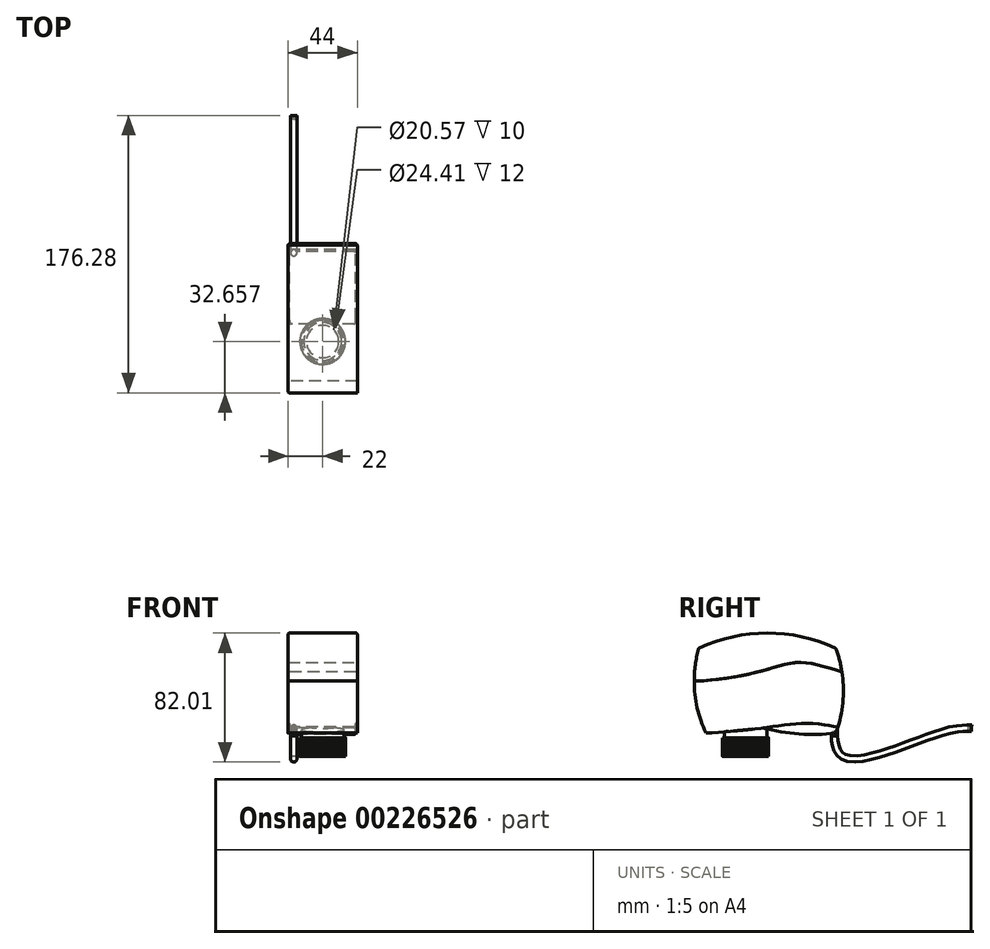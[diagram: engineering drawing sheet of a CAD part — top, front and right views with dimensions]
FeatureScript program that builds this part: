
annotation { "Feature Type Name" : "Feature", "Feature Type Description" : "" }
export const myFeature = defineFeature(function(context is Context, id is Id, definition is map)
    precondition{}
    {
        {
            var Q0;
            Q0=qCreatedBy(makeId("Right.planeOp"),FACE);
            var sketch = newSketch(context, id + "F0", { "sketchPlane" : qUnion([Q0])});
            skArc(sketch, "E0", {"start": v(-40.88, 27.1) * mm, "mid": v(-43.48, -0.31) * mm, "end": v(-36.3, -26.9) * mm});
            skArc(sketch, "E1", {"start": v(46.12, 27.1) * mm, "mid": v(2.62, 36.69) * mm, "end": v(-40.88, 27.1) * mm});
            skArc(sketch, "E2", {"start": v(46.12, -26.9) * mm, "mid": v(50.98, 0.1) * mm, "end": v(46.12, 27.1) * mm});
            skLineSegment(sketch, "E3", {"start": v(-36.3, -26.9) * mm, "end": v(46.12, -26.9) * mm, "construction": true});
            skFitSpline(sketch, "E4", {"points": [v(-43.75, 6.1) * mm, v(0, 12.84) * mm, v(24.24, 17.97) * mm, v(50.05, 12.1) * mm], "startDerivative": vector(120.11, 3.83) * mm, "endDerivative": vector(83.49, -22.87) * mm});
            skFitSpline(sketch, "E5", {"points": [v(-36.3, -26.9) * mm, v(0, -23.58) * mm, v(32.41, -20.85) * mm, v(47.43, -23.06) * mm, v(47.45, -23) * mm], "startDerivative": vector(96.75, 6.97) * mm, "endDerivative": vector(-0.56, 4.09) * mm});
            skSolve(sketch);
        }
        {
            var Q0;
            {var subQ0=sQuery(id+"F0.wireOp",EDGE,"E1");Q0=makeQuery(id+"F0.imprint","IMPRINT",FACE,{"disambiguationData":[TD([[makeQuery(id+"F0.imprint","IMPRINT",EDGE,{"derivedFrom":subQ0}),1.0]])]});}
            extrude(context, id + "F1", {"entities" : qUnion([Q0]), "endBound" : BoundingType.SYMMETRIC, "depth" : 44 * mm});
        }
        {
            var Q0;
            {var subQ0=sQuery(id+"F0.wireOp",EDGE,"E4");Q0=makeQuery(id+"F0.imprint","IMPRINT",FACE,{"disambiguationData":[TD([[makeQuery(id+"F0.imprint","IMPRINT",EDGE,{"derivedFrom":subQ0}),-1.0]])]});}
            extrude(context, id + "F2", {"entities" : qUnion([Q0]), "endBound" : BoundingType.SYMMETRIC, "depth" : 44 * mm});
        }
        {
            var Q0;
            Q0=qCreatedBy(makeId("Right.planeOp"),FACE);
            var sketch = newSketch(context, id + "F3", { "sketchPlane" : qUnion([Q0])});
            skArc(sketch, "E6", {"start": v(0, -23.58) * mm, "mid": v(22.9, -27.46) * mm, "end": v(46.12, -26.9) * mm});
            skLineSegment(sketch, "E7", {"start": v(46.12, -26.9) * mm, "end": v(47.43, -23.06) * mm});
            skLineSegment(sketch, "E8", {"start": v(0, -23.58) * mm, "end": v(31.62, -13.02) * mm});
            skLineSegment(sketch, "E9", {"start": v(31.62, -13.02) * mm, "end": v(47.43, -23.06) * mm});
            skSolve(sketch);
        }
        {
            var Q0;
            Q0 = qSketchRegion(id + "F3", true);
            extrude(context, id + "F4", {"entities" : qUnion([Q0]), "operationType" : NewBodyOperationType.ADD, "endBound" : BoundingType.SYMMETRIC, "depth" : 42 * mm});
        }
        {
            var Q0;
            Q0=qCreatedBy(makeId("Right.planeOp"),FACE);
            var sketch = newSketch(context, id + "F5", { "sketchPlane" : qUnion([Q0])});
            skLineSegment(sketch, "E10", {"start": v(-11.1, 0.62) * mm, "end": v(-11.1, -57.57) * mm, "construction": true});
            skLineSegment(sketch, "E11", {"start": v(2.4, -19.81) * mm, "end": v(2.4, -29.81) * mm});
            skLineSegment(sketch, "E12", {"start": v(2.4, -29.81) * mm, "end": v(-11.1, -29.81) * mm});
            skLineSegment(sketch, "E13", {"start": v(-11.1, -29.81) * mm, "end": v(-11.1, -19.81) * mm});
            skLineSegment(sketch, "E14", {"start": v(-11.1, -19.81) * mm, "end": v(2.4, -19.81) * mm});
            skSolve(sketch);
        }
        {
            var Q0;
            Q0 = qSketchRegion(id + "F5", true);
            var Q1;
            Q1=sQuery(id+"F5.wireOp",EDGE,"E10");
            revolve(context, id + "F6", {"operationType" : NewBodyOperationType.ADD, "entities" : qUnion([Q0]), "axis" : qUnion([Q1]), "revolveType" : RevolveType.FULL});
        }
        {
            var Q0;
            Q0=makeQuery(id+"F6.opRevolve","SWEPT_FACE",FACE,{"disambiguationData":[OSD([sQuery(id+"F5.wireOp",EDGE,"E12")])]});
            var sketch = newSketch(context, id + "F7", { "sketchPlane" : qUnion([Q0])});
            skCircle(sketch, "E15", {"center": v(0, 11.1) * mm, "radius": 12.02 * mm});
            skCircle(sketch, "E16", {"center": v(0, 11.1) * mm, "radius": 10.28 * mm});
            skSolve(sketch);
        }
        {
            var Q0;
            Q0 = qSketchRegion(id + "F7", true);
            extrude(context, id + "F8", {"entities" : qUnion([Q0]), "operationType" : NewBodyOperationType.ADD, "depth" : 10 * mm});
        }
        {
            var Q0;
            Q0=makeQuery(id+"F8.boolean.opBoolean","SPLIT",FACE,{"disambiguationData":[TD([makeQuery(id+"F6.opRevolve","SWEPT_FACE",FACE,{"disambiguationData":[OSD([sQuery(id+"F5.wireOp",EDGE,"E11")])]})])],"derivedFrom":makeQuery(id+"F6.opRevolve","SWEPT_FACE",FACE,{"disambiguationData":[OSD([sQuery(id+"F5.wireOp",EDGE,"E12")])]})});
            var sketch = newSketch(context, id + "F9", { "sketchPlane" : qUnion([Q0])});
            skCircle(sketch, "E17", {"center": v(0, 11.1) * mm, "radius": 12.2 * mm});
            skCircle(sketch, "E18", {"center": v(0, 11.1) * mm, "radius": 14.18 * mm});
            skArc(sketch, "E19", {"start": v(0.43, 25.27) * mm, "mid": v(0, 25.68) * mm, "end": v(-0.43, 25.27) * mm});
            skSolve(sketch);
        }
        {
            var Q0;
            Q0 = qSketchRegion(id + "F9", true);
            extrude(context, id + "F10", {"entities" : qUnion([Q0]), "depth" : 12 * mm});
        }
        {
            var Q0;
            Q0=makeQuery(id+"F10.opExtrude","SWEPT_BODY",BODY,{"disambiguationData":[OSD([sQuery(id+"F9.wireOp",EDGE,"E17"),sQuery(id+"F9.wireOp",EDGE,"E18"),sQuery(id+"F9.wireOp",EDGE,"E19")])]});
            var Q1;
            Q1=makeQuery(id+"F10.opExtrude","CAP_EDGE",EDGE,{"disambiguationData":[OSD([sQuery(id+"F9.wireOp",EDGE,"E17")])],"isStart":false});
            circularPattern(context, id + "F11", {"operationType" : NewBodyOperationType.ADD, "entities" : qUnion([Q0]), "axis" : qUnion([Q1]), "angle" : 360 * degree, "instanceCount" : 100, "equalSpace" : true});
        }
        {
            var Q0;
            Q0=qCreatedBy(makeId("Top.planeOp"),FACE);
            var sketch = newSketch(context, id + "F12", { "sketchPlane" : qUnion([Q0])});
            skCircle(sketch, "E20", {"center": v(-18.32, 45.24) * mm, "radius": 2 * mm});
            skSolve(sketch);
        }
        {
            var Q0;
            Q0 = qSketchRegion(id + "F12", true);
            extrude(context, id + "F13", {"entities" : qUnion([Q0]), "operationType" : NewBodyOperationType.ADD, "oppositeDirection" : true, "depth" : 28.6 * mm});
        }
        {
            var Q0;
            Q0=makeQuery(id+"F13.opExtrude","CAP_FACE",FACE,{"disambiguationData":[OSD([sQuery(id+"F12.wireOp",EDGE,"E20")])],"isStart":false});
            var sketch = newSketch(context, id + "F14", { "sketchPlane" : qUnion([Q0])});
            skLineSegment(sketch, "E21", {"start": v(-18.32, -45.24) * mm, "end": v(-20.32, -45.24) * mm, "construction": true});
            skLineSegment(sketch, "E22", {"start": v(-18.32, -45.24) * mm, "end": v(-16.32, -45.24) * mm, "construction": true});
            skSolve(sketch);
        }
        {
            var Q0;
            Q0=sQuery(id+"F14.wireOp",VERTEX,"E21.end");
            var Q1;
            Q1=sQuery(id+"F14.wireOp",VERTEX,"E22.end");
            cPlane(context, id + "F15", {"entities" : qUnion([Q0, Q1]), "cplaneType" : CPlaneType.MID_PLANE, "offset" : 25 * mm, "width" : 150 * mm, "height" : 150 * mm});
        }
        {
            var Q0;
            Q0=qCreatedBy(id+"F15.planeOp",FACE);
            var sketch = newSketch(context, id + "F16", { "sketchPlane" : qUnion([Q0])});
            skFitSpline(sketch, "E23", {"points": [v(45.24, -28.6) * mm, v(54.67, -43.14) * mm, v(106.35, -28.78) * mm, v(132.32, -23.82) * mm], "startDerivative": vector(5.98, -103.82) * mm, "endDerivative": vector(86.83, -3.78) * mm});
            skSolve(sketch);
        }
        {
            var Q0;
            Q0=makeQuery(id+"F14.imprint","IMPRINT",FACE,{"disambiguationData":[TD([[makeQuery(id+"F14.imprint","IMPRINT",EDGE,{"derivedFrom":makeQuery(id+"F13.opExtrude","CAP_EDGE",EDGE,{"disambiguationData":[OSD([sQuery(id+"F12.wireOp",EDGE,"E20")])],"isStart":false})}),-1.0]])]});
            var Q1;
            Q1=sQuery(id+"F16.wireOp",EDGE,"E23");
            sweep(context, id + "F17", {"operationType" : NewBodyOperationType.ADD, "profiles" : qUnion([Q0]), "path" : qUnion([Q1])});
        }
        {
            var Q0;
            Q0=makeQuery(id+"F17.opSweep","CAP_FACE",FACE,{"disambiguationData":[OSD([sQuery(id+"F12.wireOp",EDGE,"E20"),sQuery(id+"F16.wireOp",VERTEX,"E23.end")])],"isStart":false});
            var sketch = newSketch(context, id + "F18", { "sketchPlane" : qUnion([Q0])});
            skCircle(sketch, "E24", {"center": v(17.64, -9.64) * mm, "radius": 0.48 * mm});
            skSolve(sketch);
        }
        {
            var Q0;
            Q0 = qSketchRegion(id + "F18", true);
            extrude(context, id + "F19", {"entities" : qUnion([Q0]), "oppositeDirection" : true, "depth" : 2 * mm});
        }
        {
            var Q0;
            Q0=makeQuery(id+"F19.opExtrude","SWEPT_BODY",BODY,{"disambiguationData":[OSD([sQuery(id+"F18.wireOp",EDGE,"E24")])]});
            var Q1;
            Q1=makeQuery(id+"F17.opSweep","CAP_EDGE",EDGE,{"disambiguationData":[OSD([sQuery(id+"F12.wireOp",EDGE,"E20"),sQuery(id+"F16.wireOp",VERTEX,"E23.end")])],"isStart":false});
            circularPattern(context, id + "F20", {"operationType" : NewBodyOperationType.REMOVE, "entities" : qUnion([Q0]), "axis" : qUnion([Q1]), "angle" : 360 * degree, "instanceCount" : 3, "equalSpace" : true});
        }
        {
            var Q0;
            Q0=makeQuery(id+"F1.opExtrude","SWEPT_FACE",FACE,{"disambiguationData":[OSD([sQuery(id+"F0.wireOp",EDGE,"E1")])]});
            var Q1;
            Q1=makeQuery(id+"F1.opExtrude","CAP_EDGE",EDGE,{"disambiguationData":[OSD([sQuery(id+"F0.wireOp",EDGE,"E0")])],"isStart":true});
            var Q2;
            Q2=makeQuery(id+"F1.opExtrude","CAP_EDGE",EDGE,{"disambiguationData":[OSD([sQuery(id+"F0.wireOp",EDGE,"E0")])],"isStart":false});
            var Q3;
            Q3=makeQuery(id+"F1.opExtrude","CAP_EDGE",EDGE,{"disambiguationData":[OSD([sQuery(id+"F0.wireOp",EDGE,"E2")])],"isStart":true});
            var Q4;
            Q4=makeQuery(id+"F1.opExtrude","CAP_EDGE",EDGE,{"disambiguationData":[OSD([sQuery(id+"F0.wireOp",EDGE,"E2")])],"isStart":false});
            var Q5;
            Q5=makeQuery(id+"F2.opExtrude","CAP_EDGE",EDGE,{"disambiguationData":[OSD([sQuery(id+"F0.wireOp",EDGE,"E2")])],"isStart":false});
            var Q6;
            Q6=makeQuery(id+"F2.opExtrude","CAP_EDGE",EDGE,{"disambiguationData":[OSD([sQuery(id+"F0.wireOp",EDGE,"E2")])],"isStart":true});
            var Q7;
            Q7=makeQuery(id+"F2.opExtrude","CAP_EDGE",EDGE,{"disambiguationData":[OSD([sQuery(id+"F0.wireOp",EDGE,"E0")])],"isStart":true});
            var Q8;
            Q8=makeQuery(id+"F4.opExtrude","CAP_EDGE",EDGE,{"disambiguationData":[OSD([sQuery(id+"F3.wireOp",EDGE,"E6")])],"isStart":true});
            var Q9;
            Q9=makeQuery(id+"F4.opExtrude","CAP_EDGE",EDGE,{"disambiguationData":[OSD([sQuery(id+"F3.wireOp",EDGE,"E6")])],"isStart":false});
            var Q10;
            Q10=makeQuery(id+"F4.opExtrude","CAP_EDGE",EDGE,{"disambiguationData":[OSD([sQuery(id+"F3.wireOp",EDGE,"E7")])],"isStart":false});
            var Q11;
            Q11=makeQuery(id+"F4.opExtrude","CAP_EDGE",EDGE,{"disambiguationData":[OSD([sQuery(id+"F3.wireOp",EDGE,"E7")])],"isStart":true});
            fillet(context, id + "F21", {"entities" : qUnion([Q0, Q1, Q2, Q3, Q4, Q5, Q6, Q7, Q8, Q9, Q10, Q11]), "radius" : 1 * mm, "tangentPropagation" : true, "allowEdgeOverflow" : false});
        }
    });
